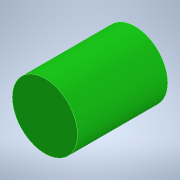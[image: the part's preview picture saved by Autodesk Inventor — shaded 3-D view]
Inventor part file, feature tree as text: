
AUTODESK INVENTOR PART (.ipt)
format: ipt  version: 2022 (Build 260153000, 153)  size: 89,600 bytes
history: native  units: mm
features: extrude x1, sketch x1
ambient origin geometry x8: Origin, YZ Plane, XZ Plane, XY Plane, X Axis, Y Axis, Z Axis, Center Point
bodies: Solid1 (feature_tree)
feature tree (2):
  extrude  "Extrusion1"  Depth=38.0mm TaperAngle=0.0deg
  sketch  "Sketch1"  dims[d0=27.5mm d1=38.0mm d2=0.0mm]
